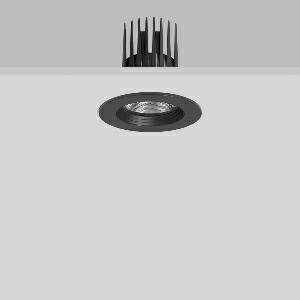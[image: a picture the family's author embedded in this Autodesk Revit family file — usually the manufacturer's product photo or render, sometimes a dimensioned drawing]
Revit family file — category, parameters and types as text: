
# Revit family: heledon_mini_e_901750_003_a088
name_source: partatom
category: Lighting Fixtures
units: mm (PartAtom-declared; Revit-internal decimal feet)

## family parameters
Cut with Voids When Loaded = No
Host = Face
Light Source = No
Part Type = Normal
Room Calculation Point = No
Round Connector Dimension = Use Diameter
Shared = No

## types (1)
- HELEDON mini E (1 x LED Modul 930, 3650 lm, 3000)
    Apparent Load = 29 VA
    Approval mark = CE
    CIE Flux Codes = 95 99 100 100 100
    Color Rendering = 90
    Color Temperature = 3000
    Default Elevation = 1800 mm
    Description = Series: HELEDON mini
Round recessed downlight. Housing: die-cast aluminium, powder-coated. Black plastic ring and recessed LED to prevent glare from the side. Optical assembly with reflector made of MIRO-Silver with 98% total light reflection for outstanding efficiency - can be changed without tools. Best colour rendering index Ra>90. Suitable for Recessed ceiling mounting. Installation without tools thanks to spring fastening system. Including separate LED converter with connecting cable 600 mm.High quality converter without flickering and stroboscopic effect. Through-wiring box (5 pole) available as accessory. The following accessories can be mounted without use of tools: interchangeable lenses, decorative glasses, honeycomb louvre, clear and frosted diffusers, white interchangeable plastic ring. 
Colour: deep black, matt (RAL 9005)
Diameter: 124 mm
Height: 3 mm
Cut-out diameter: 114 mm
Recess height: 170 mm
Luminaire: recess height: 120 mm
Lamp: LED
Socket: without socket
Colour temperature: 3000K
Colour rendering index (CRI): 92
System power: 29 W
Rated luminous flux: 3650 lm
Luminous efficiency: 126 lm/W
Control gear: Regulated power supply
Protection class: II
Type of protection: IP 20
    Height = 0 mm  [stored 0 ft]
    Lamp = 1 x LED Modul 930
    Lamp Light Flux = 3650 lm
    Lamp count = 1
    Length = 124 mm  [stored 0.406824 ft]
    Lifetime = 50000 h
    Luminous efficacy = 126 lm/W
    Manufacturer = RZB
    ModVariant = No
    Model = 901750.003
    Mounting Place = Ceiling
    Mounting Type = Recessed
    Number of Poles = 1
    OnlyDefault = Yes
    Power Factor = 1
    Product Name = HELEDON mini E
    Product group = Recessed downlights
    ProductGroupID = 402
    Protection Class = Protection class II
    Protection Degree = IP 20
    RLX_Detail_Level = 1
    RLX_Emergency_Light_Flux = 0 lm
    RLX_Emergency_Type = 0
    RLX_Emergency_Type_DB = No
    RlxData = <blob elided: 127501 chars, md5=db4113ce>
    Socket = socket
    Standby Power = 0 W
    System Light Flux = 3650 lm
    System Power = 29 W
    Type Comments = Product without accessories
    Type Image = 901657.003.jpg
    URL = http://relux.com
    VarID = ---
    Voltage = 230 V
    Voltage Range = 220-240 V
    Weight = 0.00 kg
    Width = 0 mm  [stored 0 ft]

note: [stored X ft] marks values corroborated as IEEE doubles in the binary element streams (Revit-internal decimal feet)

## geometry (parser evidence)
native form markers: Blend x4, Sweep x11
no freeform markers — native parametric forms only
